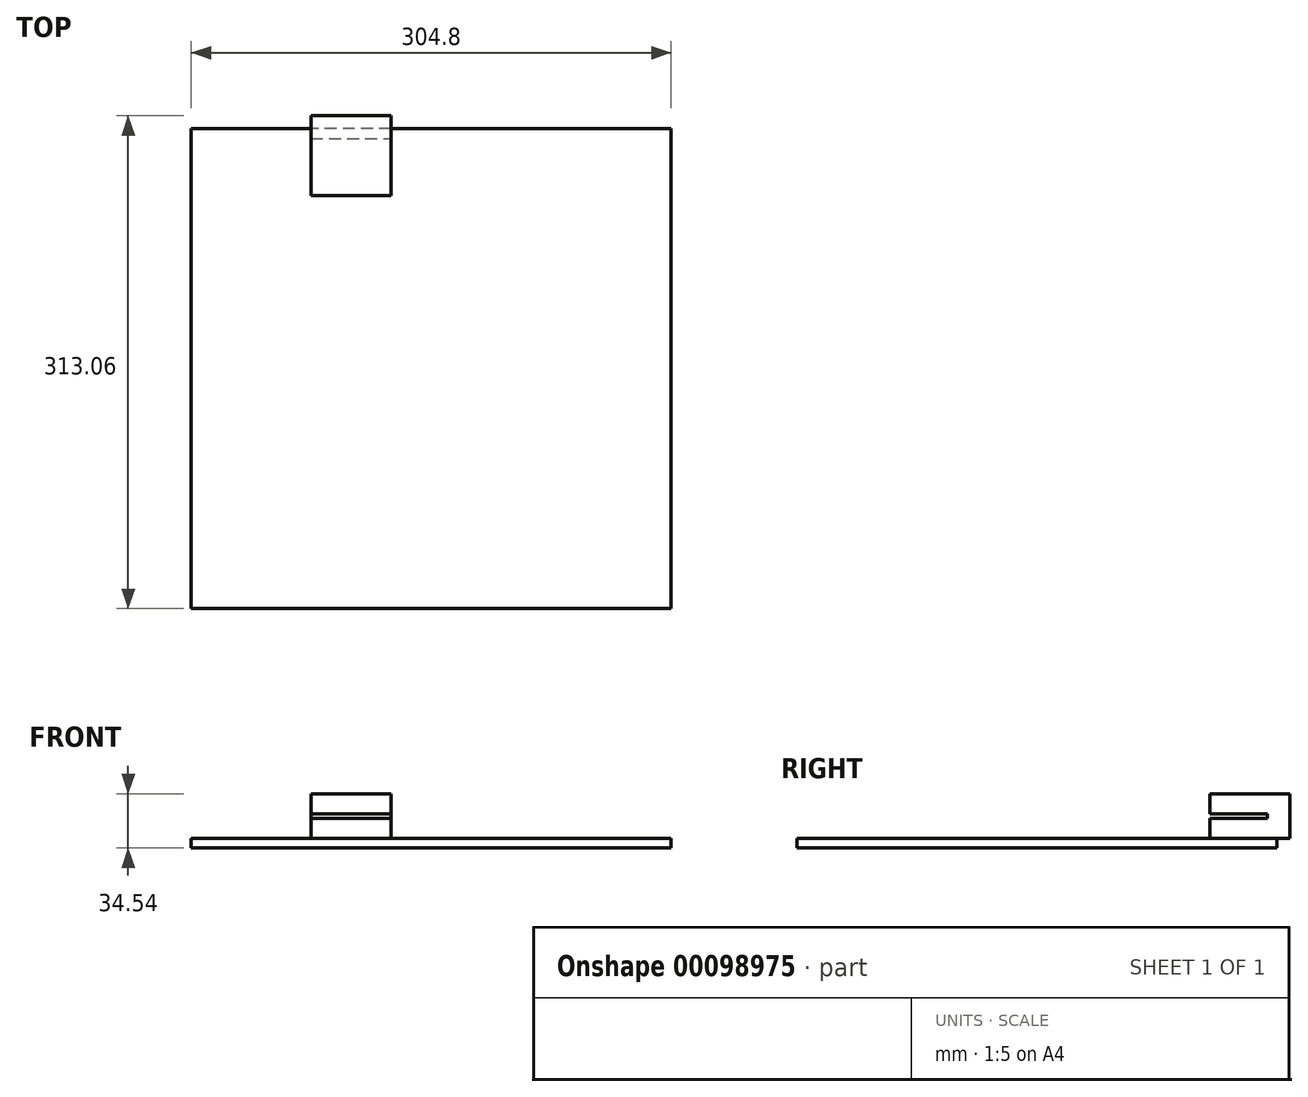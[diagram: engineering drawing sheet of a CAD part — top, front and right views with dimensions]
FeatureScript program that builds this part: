
annotation { "Feature Type Name" : "Feature", "Feature Type Description" : "" }
export const myFeature = defineFeature(function(context is Context, id is Id, definition is map)
    precondition{}
    {
        {
            var Q0;
            Q0=qCreatedBy(makeId("Top.planeOp"),FACE);
            var sketch = newSketch(context, id + "F0", { "sketchPlane" : qUnion([Q0])});
            skLineSegment(sketch, "E0.bottom", {"start": v(152.4, 152.4) * mm, "end": v(-152.4, 152.4) * mm});
            skLineSegment(sketch, "E0.top", {"start": v(152.4, -152.4) * mm, "end": v(-152.4, -152.4) * mm});
            skLineSegment(sketch, "E0.left", {"start": v(152.4, 152.4) * mm, "end": v(152.4, -152.4) * mm});
            skLineSegment(sketch, "E0.right", {"start": v(-152.4, 152.4) * mm, "end": v(-152.4, -152.4) * mm});
            skPoint(sketch, "E0.middle", {"position": v(0, 0) * mm});
            skSolve(sketch);
        }
        {
            var Q0;
            Q0 = qSketchRegion(id + "F0", true);
            extrude(context, id + "F1", {"entities" : qUnion([Q0]), "depth" : 6.1 * mm});
        }
        {
            var Q0;
            Q0=makeQuery(id+"F1.opExtrude","CAP_FACE",FACE,{"disambiguationData":[OSD([sQuery(id+"F0.wireOp",EDGE,"E0.bottom"),sQuery(id+"F0.wireOp",EDGE,"E0.top"),sQuery(id+"F0.wireOp",EDGE,"E0.left"),sQuery(id+"F0.wireOp",EDGE,"E0.right")])],"isStart":false});
            var sketch = newSketch(context, id + "F2", { "sketchPlane" : qUnion([Q0])});
            skLineSegment(sketch, "E1.bottom", {"start": v(-25.62, 109.86) * mm, "end": v(-76.42, 109.86) * mm});
            skLineSegment(sketch, "E1.top", {"start": v(-25.62, 160.66) * mm, "end": v(-76.42, 160.66) * mm});
            skLineSegment(sketch, "E1.left", {"start": v(-25.62, 109.86) * mm, "end": v(-25.62, 160.66) * mm});
            skLineSegment(sketch, "E1.right", {"start": v(-76.42, 109.86) * mm, "end": v(-76.42, 160.66) * mm});
            skPoint(sketch, "E1.middle", {"position": v(-51.02, 135.26) * mm});
            skSolve(sketch);
        }
        {
            var Q0;
            Q0 = qSketchRegion(id + "F2", true);
            extrude(context, id + "F3", {"entities" : qUnion([Q0]), "depth" : 12.7 * mm});
        }
        {
            var Q0;
            Q0=makeQuery(id+"F3.opExtrude","CAP_FACE",FACE,{"disambiguationData":[OSD([sQuery(id+"F2.wireOp",EDGE,"E1.bottom"),sQuery(id+"F2.wireOp",EDGE,"E1.top"),sQuery(id+"F2.wireOp",EDGE,"E1.left"),sQuery(id+"F2.wireOp",EDGE,"E1.right")])],"isStart":false});
            var sketch = newSketch(context, id + "F4", { "sketchPlane" : qUnion([Q0])});
            skLineSegment(sketch, "E2.bottom", {"start": v(-76.42, 146.3) * mm, "end": v(-25.62, 146.3) * mm});
            skLineSegment(sketch, "E2.top", {"start": v(-76.42, 160.66) * mm, "end": v(-25.62, 160.66) * mm});
            skLineSegment(sketch, "E2.left", {"start": v(-76.42, 146.3) * mm, "end": v(-76.42, 160.66) * mm});
            skLineSegment(sketch, "E2.right", {"start": v(-25.62, 146.3) * mm, "end": v(-25.62, 160.66) * mm});
            skSolve(sketch);
        }
        {
            var Q0;
            Q0 = qSketchRegion(id + "F4", true);
            extrude(context, id + "F5", {"entities" : qUnion([Q0]), "operationType" : NewBodyOperationType.ADD, "depth" : 3.05 * mm});
        }
        {
            var Q0;
            Q0=makeQuery(id+"F5.opExtrude","CAP_FACE",FACE,{"disambiguationData":[OSD([sQuery(id+"F4.wireOp",EDGE,"E2.bottom"),sQuery(id+"F4.wireOp",EDGE,"E2.top"),sQuery(id+"F4.wireOp",EDGE,"E2.left"),sQuery(id+"F4.wireOp",EDGE,"E2.right")])],"isStart":false});
            var sketch = newSketch(context, id + "F6", { "sketchPlane" : qUnion([Q0])});
            skLineSegment(sketch, "E3.bottom", {"start": v(-76.42, 160.66) * mm, "end": v(-25.62, 160.66) * mm});
            skLineSegment(sketch, "E3.top", {"start": v(-76.42, 109.86) * mm, "end": v(-25.62, 109.86) * mm});
            skLineSegment(sketch, "E3.left", {"start": v(-76.42, 160.66) * mm, "end": v(-76.42, 109.86) * mm});
            skLineSegment(sketch, "E3.right", {"start": v(-25.62, 160.66) * mm, "end": v(-25.62, 109.86) * mm});
            skSolve(sketch);
        }
        {
            var Q0;
            Q0 = qSketchRegion(id + "F6", true);
            extrude(context, id + "F7", {"entities" : qUnion([Q0]), "operationType" : NewBodyOperationType.ADD, "depth" : 12.7 * mm});
        }
    });
